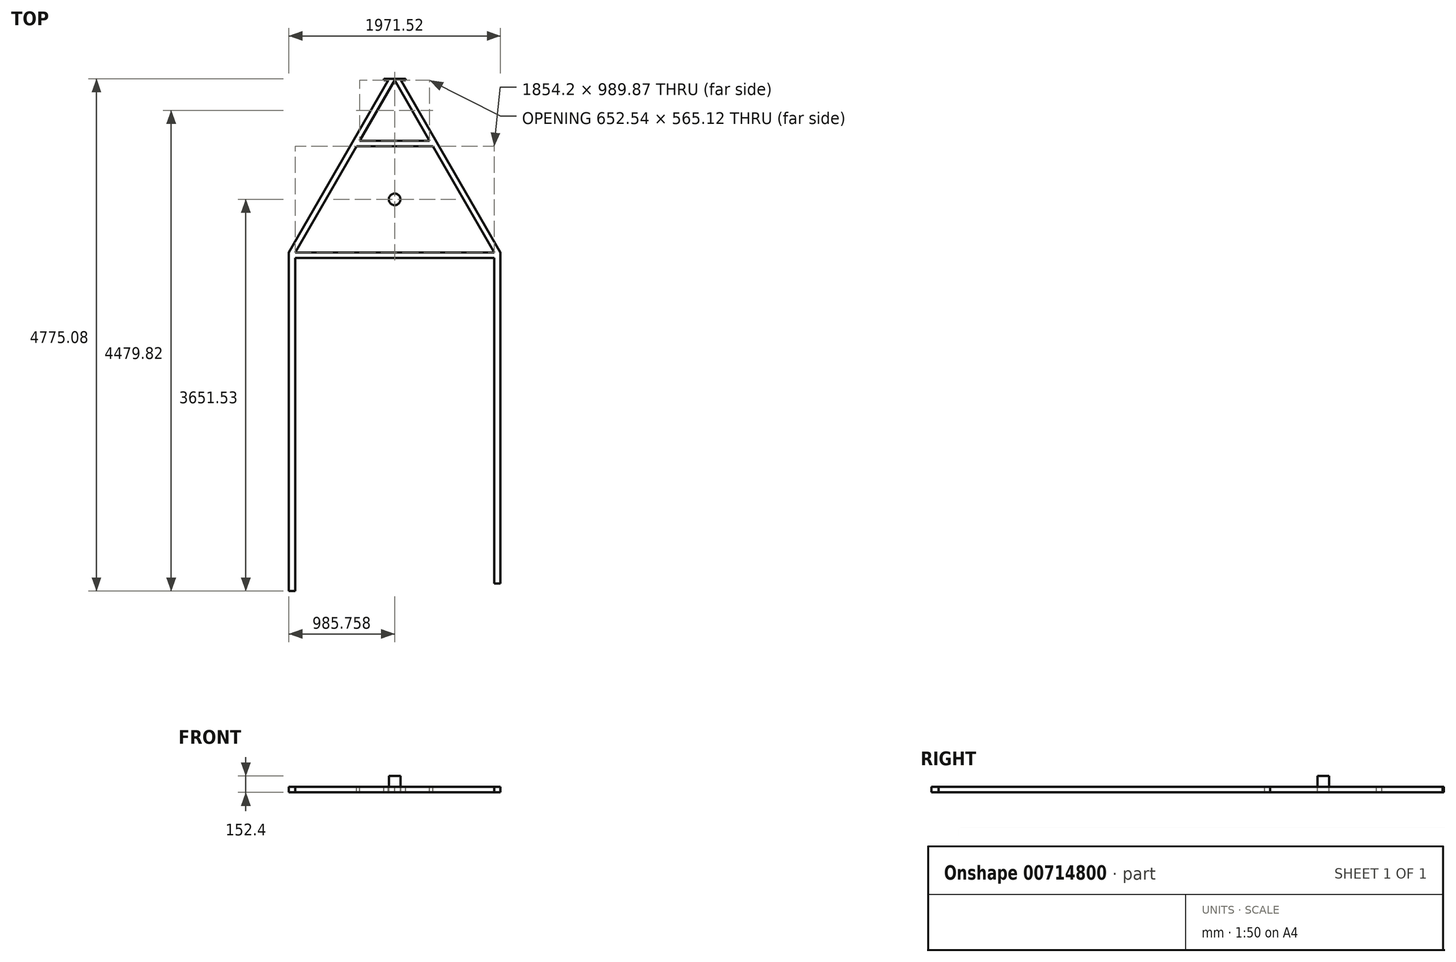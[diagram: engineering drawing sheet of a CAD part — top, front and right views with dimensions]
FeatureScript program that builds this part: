
annotation { "Feature Type Name" : "Feature", "Feature Type Description" : "" }
export const myFeature = defineFeature(function(context is Context, id is Id, definition is map)
    precondition{}
    {
        {
            var Q0;
            Q0=qCreatedBy(makeId("Top.planeOp"),FACE);
            var sketch = newSketch(context, id + "F0", { "sketchPlane" : qUnion([Q0])});
            skLineSegment(sketch, "E0", {"start": v(-864.35, 203.77) * mm, "end": v(989.85, 203.77) * mm});
            skLineSegment(sketch, "E1", {"start": v(989.85, 203.77) * mm, "end": v(62.75, 1809.56) * mm});
            skLineSegment(sketch, "E2", {"start": v(62.75, 1809.56) * mm, "end": v(-864.35, 203.77) * mm});
            skLineSegment(sketch, "E3", {"start": v(-864.35, 152.97) * mm, "end": v(989.85, 152.97) * mm});
            skLineSegment(sketch, "E4", {"start": v(989.85, 152.97) * mm, "end": v(989.85, 203.77) * mm});
            skLineSegment(sketch, "E5", {"start": v(-864.35, 203.77) * mm, "end": v(-864.35, 152.97) * mm});
            skLineSegment(sketch, "E6", {"start": v(4.09, 1809.56) * mm, "end": v(-923.01, 203.77) * mm});
            skLineSegment(sketch, "E7", {"start": v(-923.01, 203.77) * mm, "end": v(-923.01, -412.82) * mm});
            skLineSegment(sketch, "E8", {"start": v(-923.01, -412.82) * mm, "end": v(-864.35, -412.82) * mm});
            skLineSegment(sketch, "E9", {"start": v(-864.35, -412.82) * mm, "end": v(-864.35, 203.77) * mm});
            skLineSegment(sketch, "E10", {"start": v(121.4, 1809.56) * mm, "end": v(1048.5, 203.77) * mm});
            skLineSegment(sketch, "E11", {"start": v(1048.5, 203.77) * mm, "end": v(1048.5, -343.7) * mm});
            skLineSegment(sketch, "E12", {"start": v(1048.5, -343.7) * mm, "end": v(989.85, -343.7) * mm});
            skLineSegment(sketch, "E13", {"start": v(989.85, -343.7) * mm, "end": v(989.85, 203.77) * mm});
            skLineSegment(sketch, "E14", {"start": v(121.4, 1809.56) * mm, "end": v(4.09, 1809.56) * mm});
            skLineSegment(sketch, "E15", {"start": v(-864.35, 203.77) * mm, "end": v(-923.01, 203.77) * mm});
            skLineSegment(sketch, "E16", {"start": v(989.85, 203.77) * mm, "end": v(1048.5, 203.77) * mm});
            skLineSegment(sketch, "E17", {"start": v(-292.85, 1193.64) * mm, "end": v(418.35, 1193.64) * mm});
            skLineSegment(sketch, "E18", {"start": v(-263.52, 1244.44) * mm, "end": v(389.02, 1244.44) * mm});
            skLineSegment(sketch, "E19.bottom", {"start": v(-36.2, 1193.64) * mm, "end": v(116.2, 1193.64) * mm});
            skLineSegment(sketch, "E20", {"start": v(62.75, 203.77) * mm, "end": v(138.95, 203.77) * mm});
            skLineSegment(sketch, "E21", {"start": v(138.95, 203.77) * mm, "end": v(138.95, 1193.64) * mm});
            skLineSegment(sketch, "E22", {"start": v(62.75, 203.77) * mm, "end": v(-13.45, 203.77) * mm});
            skLineSegment(sketch, "E23", {"start": v(-13.45, 203.77) * mm, "end": v(-13.45, 1193.64) * mm});
            skLineSegment(sketch, "E24", {"start": v(62.75, 1809.56) * mm, "end": v(62.75, 203.77) * mm, "construction": true});
            skCircle(sketch, "E25", {"center": v(62.75, 698.7) * mm, "radius": 53.98 * mm});
            skLineSegment(sketch, "E26", {"start": v(62.75, 1809.56) * mm, "end": v(164.35, 1809.56) * mm});
            skLineSegment(sketch, "E27", {"start": v(164.35, 1809.56) * mm, "end": v(164.35, 1822.26) * mm});
            skLineSegment(sketch, "E28", {"start": v(164.35, 1822.26) * mm, "end": v(-38.85, 1822.26) * mm});
            skLineSegment(sketch, "E29", {"start": v(-38.85, 1822.26) * mm, "end": v(-38.85, 1809.56) * mm});
            skLineSegment(sketch, "E30", {"start": v(-38.85, 1809.56) * mm, "end": v(62.75, 1809.56) * mm});
            skSolve(sketch);
        }
        {
            var Q0;
            Q0=makeQuery(id+"F0.imprint","IMPRINT",FACE,{"disambiguationData":[TD([[makeQuery(id+"F0.imprint","IMPRINT",EDGE,{"derivedFrom":sQuery(id+"F0.wireOp",EDGE,"E7")}),1.0]])]});
            var Q1;
            Q1=makeQuery(id+"F0.imprint","IMPRINT",FACE,{"disambiguationData":[TD([[makeQuery(id+"F0.imprint","IMPRINT",EDGE,{"derivedFrom":sQuery(id+"F0.wireOp",EDGE,"E11")}),-1.0]])]});
            var Q2;
            {var subQ0=sQuery(id+"F0.wireOp",EDGE,"E10");Q2=makeQuery(id+"F0.imprint","IMPRINT",FACE,{"disambiguationData":[TD([[makeQuery(id+"F0.imprint","IMPRINT",EDGE,{"derivedFrom":subQ0}),-1.0]])]});}
            var Q3;
            {var subQ7=sQuery(id+"F0.wireOp",EDGE,"E18");Q3=makeQuery(id+"F0.imprint","IMPRINT",FACE,{"disambiguationData":[TD([[makeQuery(id+"F0.imprint","IMPRINT",EDGE,{"derivedFrom":subQ7}),-1.0]])]});}
            var Q4;
            {var subQ3=sQuery(id+"F0.wireOp",EDGE,"E3");Q4=makeQuery(id+"F0.imprint","IMPRINT",FACE,{"disambiguationData":[TD([[makeQuery(id+"F0.imprint","IMPRINT",EDGE,{"derivedFrom":subQ3}),1.0]])]});}
            var Q5;
            Q5=makeQuery(id+"F0.imprint","IMPRINT",FACE,{"disambiguationData":[TD([[makeQuery(id+"F0.imprint","IMPRINT",EDGE,{"derivedFrom":sQuery(id+"F0.wireOp",EDGE,"E20")}),1.0]])]});
            var Q6;
            {var subQ0=sQuery(id+"F0.wireOp",EDGE,"E6");Q6=makeQuery(id+"F0.imprint","IMPRINT",FACE,{"disambiguationData":[TD([[makeQuery(id+"F0.imprint","IMPRINT",EDGE,{"derivedFrom":subQ0}),1.0]])]});}
            var Q7;
            Q7=makeQuery(id+"F0.imprint","IMPRINT",FACE,{"disambiguationData":[TD([[makeQuery(id+"F0.imprint","IMPRINT",EDGE,{"derivedFrom":sQuery(id+"F0.wireOp",EDGE,"E25")}),1.0]])]});
            var Q8;
            {var subQ0=sQuery(id+"F0.wireOp",EDGE,"E27");Q8=makeQuery(id+"F0.imprint","IMPRINT",FACE,{"disambiguationData":[TD([[makeQuery(id+"F0.imprint","IMPRINT",EDGE,{"derivedFrom":subQ0}),1.0]])]});}
            var Q9;
            Q9=sQuery(id+"F0.wireOp",EDGE,"E18");
            var Q10;
            Q10=sQuery(id+"F0.wireOp",EDGE,"E11");
            var Q11;
            Q11=sQuery(id+"F0.wireOp",EDGE,"E23");
            var Q12;
            Q12=sQuery(id+"F0.wireOp",EDGE,"E25");
            var Q13;
            Q13=sQuery(id+"F0.wireOp",EDGE,"E3");
            var Q14;
            Q14=sQuery(id+"F0.wireOp",EDGE,"E9");
            var Q15;
            Q15=sQuery(id+"F0.wireOp",EDGE,"E2");
            var Q16;
            Q16=sQuery(id+"F0.wireOp",EDGE,"E1");
            var Q17;
            Q17=sQuery(id+"F0.wireOp",EDGE,"E10");
            var Q18;
            Q18=sQuery(id+"F0.wireOp",EDGE,"E13");
            var Q19;
            Q19=sQuery(id+"F0.wireOp",EDGE,"E7");
            var Q20;
            Q20=sQuery(id+"F0.wireOp",EDGE,"E0");
            var Q21;
            Q21=sQuery(id+"F0.wireOp",EDGE,"E21");
            var Q22;
            Q22=sQuery(id+"F0.wireOp",EDGE,"E6");
            var Q23;
            Q23=sQuery(id+"F0.wireOp",EDGE,"E17");
            var Q24;
            Q24=sQuery(id+"F0.wireOp",EDGE,"E19.bottom");
            var Q25;
            Q25=sQuery(id+"F0.wireOp",EDGE,"E27");
            var Q26;
            Q26=sQuery(id+"F0.wireOp",EDGE,"E12");
            var Q27;
            Q27=sQuery(id+"F0.wireOp",EDGE,"E14");
            var Q28;
            Q28=sQuery(id+"F0.wireOp",EDGE,"E22");
            var Q29;
            Q29=sQuery(id+"F0.wireOp",EDGE,"E5");
            var Q30;
            Q30=sQuery(id+"F0.wireOp",EDGE,"E8");
            var Q31;
            Q31=sQuery(id+"F0.wireOp",EDGE,"E29");
            var Q32;
            Q32=sQuery(id+"F0.wireOp",EDGE,"E26");
            var Q33;
            Q33=sQuery(id+"F0.wireOp",EDGE,"E20");
            var Q34;
            Q34=sQuery(id+"F0.wireOp",EDGE,"E30");
            var Q35;
            Q35=sQuery(id+"F0.wireOp",EDGE,"E28");
            var Q36;
            Q36=sQuery(id+"F0.wireOp",EDGE,"E4");
            var Q37;
            Q37=sQuery(id+"F0.wireOp",EDGE,"E16");
            var Q38;
            Q38=sQuery(id+"F0.wireOp",EDGE,"E15");
            extrude(context, id + "F1", {"entities" : qUnion([Q0, Q1, Q2, Q3, Q4, Q5, Q6, Q7, Q8]), "surfaceEntities" : qUnion([Q9, Q10, Q11, Q12, Q13, Q14, Q15, Q16, Q17, Q18, Q19, Q20, Q21, Q22, Q23, Q24, Q25, Q26, Q27, Q28, Q29, Q30, Q31, Q32, Q33, Q34, Q35, Q36, Q37, Q38]), "oppositeDirection" : true, "depth" : 152.4 * mm, "offsetDistance" : 25.4 * mm});
        }
        {
            var Q0;
            Q0=makeQuery(id+"F1.opExtrude","CAP_FACE",FACE,{"disambiguationData":[OSD([sQuery(id+"F0.wireOp",EDGE,"E0"),sQuery(id+"F0.wireOp",EDGE,"E1"),sQuery(id+"F0.wireOp",EDGE,"E2"),sQuery(id+"F0.wireOp",EDGE,"E3"),sQuery(id+"F0.wireOp",EDGE,"E6"),sQuery(id+"F0.wireOp",EDGE,"E7"),sQuery(id+"F0.wireOp",EDGE,"E8"),sQuery(id+"F0.wireOp",EDGE,"E9"),sQuery(id+"F0.wireOp",EDGE,"E10"),sQuery(id+"F0.wireOp",EDGE,"E11"),sQuery(id+"F0.wireOp",EDGE,"E12"),sQuery(id+"F0.wireOp",EDGE,"E13"),sQuery(id+"F0.wireOp",EDGE,"E17"),sQuery(id+"F0.wireOp",EDGE,"E18"),sQuery(id+"F0.wireOp",EDGE,"E19.bottom"),sQuery(id+"F0.wireOp",EDGE,"E21"),sQuery(id+"F0.wireOp",EDGE,"E23"),sQuery(id+"F0.wireOp",EDGE,"E26"),sQuery(id+"F0.wireOp",EDGE,"E27"),sQuery(id+"F0.wireOp",EDGE,"E28"),sQuery(id+"F0.wireOp",EDGE,"E29"),sQuery(id+"F0.wireOp",EDGE,"E30")])],"isStart":true});
            var sketch = newSketch(context, id + "F2", { "sketchPlane" : qUnion([Q0])});
            skLineSegment(sketch, "E31", {"start": v(138.95, 1193.64) * mm, "end": v(-13.45, 1193.64) * mm});
            skLineSegment(sketch, "E32", {"start": v(138.95, 203.77) * mm, "end": v(-13.45, 203.77) * mm});
            skLineSegment(sketch, "E33", {"start": v(-13.45, 203.77) * mm, "end": v(-13.45, 1193.64) * mm});
            skLineSegment(sketch, "E34", {"start": v(138.95, 1193.64) * mm, "end": v(138.95, 203.77) * mm});
            skSolve(sketch);
        }
        {
            var Q0;
            Q0=makeQuery(id+"F2.imprint","IMPRINT",FACE,{"disambiguationData":[TD([[makeQuery(id+"F2.imprint","IMPRINT",EDGE,{"derivedFrom":sQuery(id+"F2.wireOp",EDGE,"E31")}),1.0]])]});
            extrude(context, id + "F3", {"entities" : qUnion([Q0]), "operationType" : NewBodyOperationType.REMOVE, "oppositeDirection" : true, "depth" : 101.6 * mm, "offsetDistance" : 25.4 * mm});
        }
        {
            var Q0;
            Q0=makeQuery(id+"F3.boolean.opBoolean","COPY",FACE,{"derivedFrom":makeQuery(id+"F3.opExtrude","CAP_FACE",FACE,{"disambiguationData":[OSD([sQuery(id+"F2.wireOp",EDGE,"E31"),sQuery(id+"F2.wireOp",EDGE,"E32"),sQuery(id+"F2.wireOp",EDGE,"E33"),sQuery(id+"F2.wireOp",EDGE,"E34")])],"isStart":false})});
            var sketch = newSketch(context, id + "F4", { "sketchPlane" : qUnion([Q0])});
            skPoint(sketch, "E35.centerSnap0", {"position": v(62.75, 203.77) * mm});
            skPoint(sketch, "E35.centerSnap1", {"position": v(138.95, 698.7) * mm});
            skCircle(sketch, "E36", {"center": v(62.75, 698.7) * mm, "radius": 53.98 * mm});
            skCircle(sketch, "E37", {"center": v(62.75, 698.7) * mm, "radius": 44.45 * mm});
            skSolve(sketch);
        }
        {
            var Q0;
            Q0=sQuery(id+"F4.wireOp",EDGE,"E37");
            var Q1;
            Q1=sQuery(id+"F4.wireOp",EDGE,"E36");
            extrude(context, id + "F5", {"bodyType" : ToolBodyType.SURFACE, "surfaceEntities" : qUnion([Q0, Q1]), "depth" : 127 * mm, "offsetDistance" : 25.4 * mm});
        }
        {
            var Q0;
            Q0=makeQuery(id+"F1.opExtrude","SWEPT_FACE",FACE,{"disambiguationData":[OSD([sQuery(id+"F0.wireOp",EDGE,"E12")])]});
            extrude(context, id + "F6", {"entities" : qUnion([Q0]), "operationType" : NewBodyOperationType.ADD, "depth" : 2540 * mm, "offsetDistance" : 25.4 * mm});
        }
        {
            var Q0;
            Q0=makeQuery(id+"F1.opExtrude","SWEPT_FACE",FACE,{"disambiguationData":[OSD([sQuery(id+"F0.wireOp",EDGE,"E8")])]});
            extrude(context, id + "F7", {"entities" : qUnion([Q0]), "operationType" : NewBodyOperationType.ADD, "depth" : 2540 * mm, "offsetDistance" : 25.4 * mm});
        }
    });
